FCSTD DOCUMENT  (FreeCAD 0.19R24291 (Git))
Label: heart_tube
License: All rights reserved
LicenseURL: http://en.wikipedia.org/wiki/All_rights_reserved
objects: Sketcher::SketchObject×4, PartDesign::Body×1
note: 5 computed .brp shape members not serialized (recipe doc carries the construction recipe); baked Part::Feature solids carry a one-line shape summary decoded from their .brp

FEATURE [Sketcher::SketchObject] Sketch
  FullyConstrained = true
  MapMode = 5
  Support = -> [XY_Plane]
  sketch-geometry (4):
    g0: ArcOfCircle CenterX=-50 CenterY=0 CenterZ=0 NormalX=0 NormalY=0 NormalZ=1 AngleXU=0 Radius=56 StartAngle=0.467146 EndAngle=3.96463
    g1: ArcOfCircle CenterX=50 CenterY=0 CenterZ=0 NormalX=0 NormalY=0 NormalZ=1 AngleXU=0 Radius=56 StartAngle=5.46015 EndAngle=8.95763
    g2: LineSegment StartX=-88.08 StartY=-41.0599 StartZ=0 EndX=0 EndY=-122.748 EndZ=0
    g3: LineSegment StartX=0 StartY=-122.748 StartZ=0 EndX=88.08 EndY=-41.0599 EndZ=0
  constraints (11):
    c: Symmetric(g0,g1,g-2)
    c: Equal(g1,g0)
    c: Coincident(g0,g1)
    c: PointOnObject(g2,g-2)
    c: Coincident(g3,g2)
    c: Tangent(g3,g1) = -1.5708
    c: Tangent(g2,g0) = -1.5708
    c: DistanceX(g0,g1) = 100
    c: PointOnObject(g1,g-1)
    c: Distance(g-1,g2) = 90
    c: Radius(g1) = 56
FEATURE [Sketcher::SketchObject] Sketch001
  FullyConstrained = true
  MapMode = 5
  Support = -> [XY_Plane]
  sketch-geometry (4):
    g0: ArcOfCircle CenterX=-50 CenterY=0 CenterZ=0 NormalX=0 NormalY=0 NormalZ=1 AngleXU=0 Radius=76 StartAngle=0.852776 EndAngle=3.96463
    g1: ArcOfCircle CenterX=50 CenterY=0 CenterZ=0 NormalX=0 NormalY=0 NormalZ=1 AngleXU=0 Radius=76 StartAngle=5.46015 EndAngle=8.572
    g2: LineSegment StartX=-101.68 StartY=-55.7241 StartZ=0 EndX=0 EndY=-150.025 EndZ=0
    g3: LineSegment StartX=0 StartY=-150.025 StartZ=0 EndX=101.68 EndY=-55.7241 EndZ=0
  constraints (11):
    c: Symmetric(g0,g1,g-2)
    c: Equal(g1,g0)
    c: Coincident(g0,g1)
    c: PointOnObject(g2,g-2)
    c: Coincident(g3,g2)
    c: Tangent(g3,g1) = -1.5708
    c: Tangent(g2,g0) = -1.5708
    c: DistanceX(g0,g1) = 100
    c: PointOnObject(g1,g-1)
    c: Distance(g-1,g2) = 110
    c: Radius(g1) = 76
FEATURE [Sketcher::SketchObject] Sketch002
  FullyConstrained = true
  MapMode = 5
  Support = -> [XY_Plane]
  sketch-geometry (4):
    g0: ArcOfCircle CenterX=-50 CenterY=0 CenterZ=0 NormalX=0 NormalY=0 NormalZ=1 AngleXU=0 Radius=74 StartAngle=0.828915 EndAngle=3.96463
    g1: ArcOfCircle CenterX=50 CenterY=0 CenterZ=0 NormalX=0 NormalY=0 NormalZ=1 AngleXU=0 Radius=74 StartAngle=5.46015 EndAngle=8.59586
    g2: LineSegment StartX=-100.32 StartY=-54.2577 StartZ=0 EndX=0 EndY=-147.297 EndZ=0
    g3: LineSegment StartX=0 StartY=-147.297 StartZ=0 EndX=100.32 EndY=-54.2577 EndZ=0
  constraints (11):
    c: Symmetric(g0,g1,g-2)
    c: Equal(g1,g0)
    c: Coincident(g0,g1)
    c: PointOnObject(g2,g-2)
    c: Coincident(g3,g2)
    c: Tangent(g3,g1) = -1.5708
    c: Tangent(g2,g0) = -1.5708
    c: DistanceX(g0,g1) = 100
    c: PointOnObject(g1,g-1)
    c: Distance(g-1,g2) = 108
    c: Radius(g1) = 74
FEATURE [Sketcher::SketchObject] Sketch003
  FullyConstrained = true
  MapMode = 5
  Support = -> [XY_Plane]
  sketch-geometry (4):
    g0: ArcOfCircle CenterX=-50 CenterY=0 CenterZ=0 NormalX=0 NormalY=0 NormalZ=1 AngleXU=0 Radius=58 StartAngle=0.531458 EndAngle=3.96463
    g1: ArcOfCircle CenterX=50 CenterY=0 CenterZ=0 NormalX=0 NormalY=0 NormalZ=1 AngleXU=0 Radius=58 StartAngle=5.46015 EndAngle=8.89332
    g2: LineSegment StartX=-89.44 StartY=-42.5263 StartZ=0 EndX=0 EndY=-125.475 EndZ=0
    g3: LineSegment StartX=0 StartY=-125.475 StartZ=0 EndX=89.44 EndY=-42.5263 EndZ=0
  constraints (11):
    c: Symmetric(g0,g1,g-2)
    c: Equal(g1,g0)
    c: Coincident(g0,g1)
    c: PointOnObject(g2,g-2)
    c: Coincident(g3,g2)
    c: Tangent(g3,g1) = -1.5708
    c: Tangent(g2,g0) = -1.5708
    c: DistanceX(g0,g1) = 100
    c: PointOnObject(g1,g-1)
    c: Distance(g-1,g2) = 92
    c: Radius(g1) = 58
FEATURE [PartDesign::Body] Body
  Group = -> [Sketch001,Sketch002,Sketch003,Sketch]
  Origin = -> Origin
